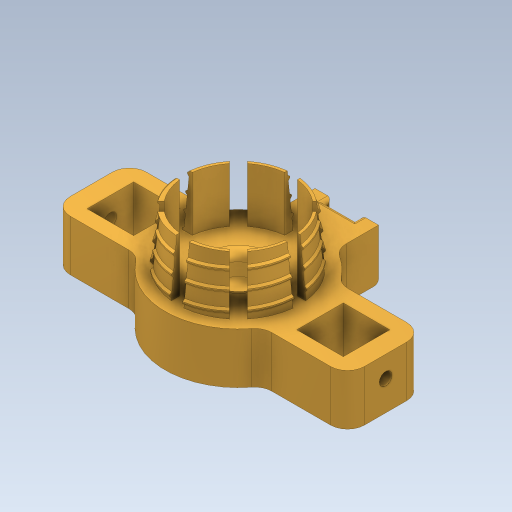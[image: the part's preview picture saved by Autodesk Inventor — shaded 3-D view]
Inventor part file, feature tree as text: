
AUTODESK INVENTOR PART (.ipt)
format: ipt  version: 2023 (Build 270158000, 158)  size: 1,005,568 bytes
history: native  units: mm
features: sketch x8, extrude x5, hole x3, fillet x3, helix x2, direct_edit x2, draft x1, mirror x1, other x1, revolve x1
ambient origin geometry x8: Origin, YZ Plane, XZ Plane, XY Plane, X Axis, Y Axis, Z Axis, Center Point
bodies: Solid1 (feature_tree)
feature tree (27):
  extrude  "Extrusion1"  Depth=12.875mm
  draft  "FaceDraft1"
  sketch  "Sketch2"  dims[d34=0.0mm d35=0.0mm d56=8.726646mm]
  helix  "Coil3"  [1 undecoded]
  helix  "Coil4"  [1 undecoded]
  direct_edit  "Direct Edit2"
  extrude  "Extrusion2"  Depth=8.726646mm
  extrude  "Extrusion13"  TaperAngle=90.0deg  [1 undecoded]
  extrude  "Extrusion14"  Depth=34.58632mm
  hole  "Hole3"  [1 undecoded]
  hole  "Hole4"  [1 undecoded]
  fillet  "Fillet11"  Radius=3.0mm
  fillet  "Fillet12"  Radius=80.0mm
  hole  "Hole5"  [1 undecoded]
  mirror  "Mirror2"
  extrude  "Extrusion15"  Depth=1.0mm
  direct_edit  "Direct Edit3"
  fillet  "Fillet13"  Radius=18.0mm
  sketch  "Sketch1"  dims[d0=25.0mm d1=26.5mm d2=12.875mm d3=0.0mm d4=1.047198mm]
  sketch  "Sketch3"  dims[d62=4.0mm d63=13.0mm d64=10.0mm d65=1.047198mm]
  sketch  "Sketch11"  dims[d66=90.0deg d67=90.0deg d68=0.0mm d69=0.0mm d70=4.0mm d71=3.0mm d72=10.0mm d73=-1.047198mm d74=90.0deg d75=90.0deg d76=0.0mm d77=0.0mm]
  sketch  "Sketch13"  dims[d79=-0.127mm d145=34.58632mm]
  sketch  "Sketch14"  dims[d150=120.0deg d151=120.0deg]
  sketch  "Sketch15"  dims[d153=21.6866mm d157=12.0mm d158=0.0mm d159=3.0mm d160=80.0mm d162=360.0deg]
  sketch  "Sketch16"  dims[d164=0.0mm d165=0.0mm d179=5.3mm d180=6.0mm d181=4.0mm d182=2.0mm d183=90.0deg d184=5.0mm d185=0.0mm d186=10.0mm d187=6.0mm d188=4.0mm d189=2.0mm d190=90.0deg d191=7.0mm d192=0.0mm d193=2.0mm d194=20.0mm d195=18.0mm d196=11.0mm d197=10.0mm d198=4.0mm d199=3.0mm d200=6.0mm d201=3.01mm d202=2.0mm d203=14.3117mm d204=8.0mm d205=0.0mm d206=15.0mm d207=10.0mm d208=7.0mm d209=10.0mm d210=1.0mm d211=0.0mm d212=-4.363323mm d213=1.0mm d109=0.5mm d110=0.872665mm d111=0.5mm d112=0.872665mm]
  other  "Size2"
  revolve  "Rotate1"  [1 undecoded]
note: 7 required parameter values undecoded (feature->parameter linkage not recoverable at this tier; creation-order binding heuristic only, values carry confidence <= 0.55)